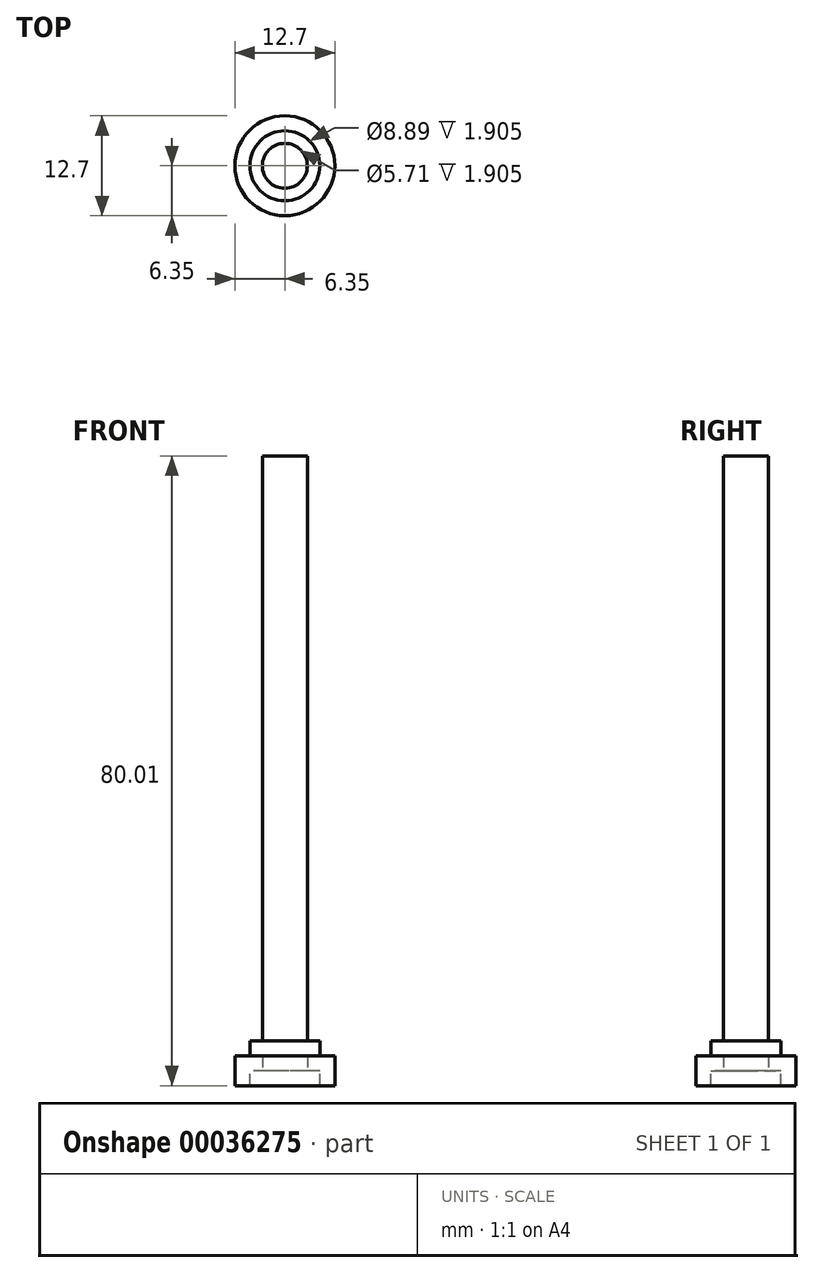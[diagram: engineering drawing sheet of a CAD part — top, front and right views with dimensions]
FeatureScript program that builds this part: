
annotation { "Feature Type Name" : "Feature", "Feature Type Description" : "" }
export const myFeature = defineFeature(function(context is Context, id is Id, definition is map)
    precondition{}
    {
        {
            var Q0;
            Q0=qCreatedBy(makeId("Top.planeOp"),FACE);
            var sketch = newSketch(context, id + "F0", { "sketchPlane" : qUnion([Q0])});
            skCircle(sketch, "E0", {"center": v(0, 0) * mm, "radius": 6.35 * mm});
            skCircle(sketch, "E1", {"center": v(0, 0) * mm, "radius": 4.45 * mm});
            skCircle(sketch, "E2", {"center": v(0, 0) * mm, "radius": 2.86 * mm});
            skSolve(sketch);
        }
        {
            var Q0;
            Q0=makeQuery(id+"F0.imprint","IMPRINT",FACE,{"disambiguationData":[TD([[makeQuery(id+"F0.imprint","IMPRINT",EDGE,{"derivedFrom":sQuery(id+"F0.wireOp",EDGE,"E2")}),1.0]])]});
            extrude(context, id + "F1", {"entities" : qUnion([Q0]), "depth" : 76.2 * mm});
        }
        {
            var Q0;
            Q0=makeQuery(id+"F0.imprint","IMPRINT",FACE,{"disambiguationData":[TD([[makeQuery(id+"F0.imprint","IMPRINT",EDGE,{"derivedFrom":sQuery(id+"F0.wireOp",EDGE,"E1")}),1.0]])]});
            extrude(context, id + "F2", {"entities" : qUnion([Q0]), "operationType" : NewBodyOperationType.ADD, "endBound" : BoundingType.SYMMETRIC, "depth" : 3.8 * mm});
        }
        {
            var Q0;
            Q0=makeQuery(id+"F0.imprint","IMPRINT",FACE,{"disambiguationData":[TD([[makeQuery(id+"F0.imprint","IMPRINT",EDGE,{"derivedFrom":sQuery(id+"F0.wireOp",EDGE,"E0")}),1.0]])]});
            extrude(context, id + "F3", {"entities" : qUnion([Q0]), "operationType" : NewBodyOperationType.ADD, "oppositeDirection" : true, "depth" : 3.8 * mm});
        }
    });
